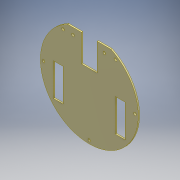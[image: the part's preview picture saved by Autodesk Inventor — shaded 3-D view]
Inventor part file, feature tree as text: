
AUTODESK INVENTOR PART (.ipt)
format: ipt  version: 2016 (Build 200138000, 138)  size: 150,528 bytes
history: native  units: mm
features: extrude x4, sketch x4, other x1
ambient origin geometry x8: Origin, YZ Plane, XZ Plane, XY Plane, X Axis, Y Axis, Z Axis, Center Point
bodies: Body1 (feature_tree)
feature tree (9):
  other  "Sólido1"
  extrude  "Extrusión1"  Depth=2.0mm TaperAngle=0.0deg
  extrude  "Extrusión2"  Depth=2.0mm
  extrude  "Extrusión3"  Depth=4.0mm
  extrude  "Extrusión4"  Depth=70.0mm
  sketch  "Boceto1"  dims[d0=150.0mm d1=18.0mm d3=15.0mm d4=50.0mm d5=15.0mm d6=50.0mm d7=40.0mm d8=40.0mm d9=2.0mm d10=0.0mm]
  sketch  "Boceto2"  dims[d11=2.0mm d12=0.0mm d13=5.0mm]
  sketch  "Boceto3"  dims[d14=4.0mm d15=4.0mm]
  sketch  "Boceto6"  dims[d16=4.0mm d17=70.0mm d18=70.0mm d19=70.0mm d20=6.0mm d21=0.0mm d22=4.0mm d23=4.0mm d24=4.0mm d25=4.0mm d26=6.0mm d27=0.0mm d28=24.0mm d29=12.0mm d33=8.0mm d34=8.0mm d36=47.0mm]
